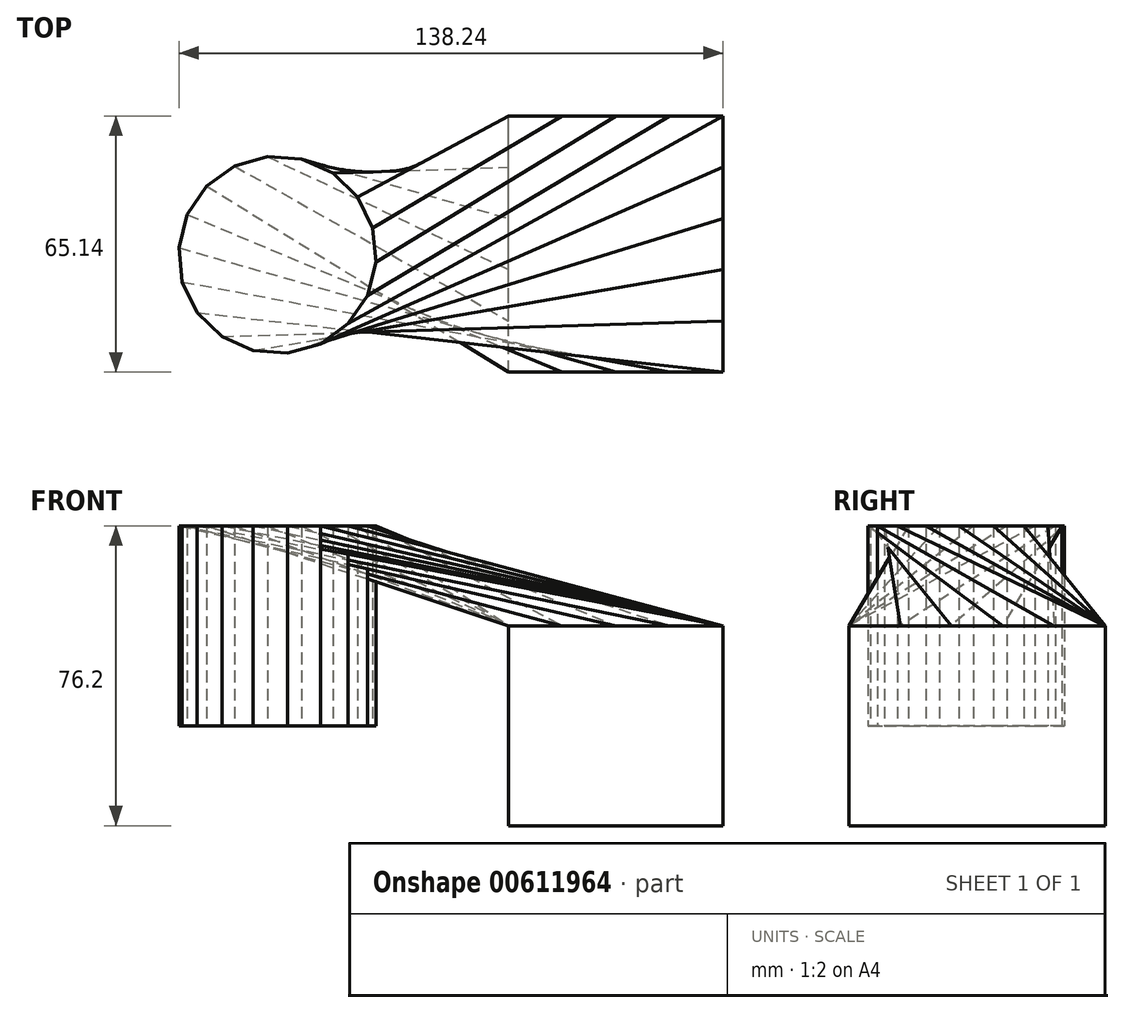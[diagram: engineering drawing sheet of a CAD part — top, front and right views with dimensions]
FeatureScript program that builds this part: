
annotation { "Feature Type Name" : "Feature", "Feature Type Description" : "" }
export const myFeature = defineFeature(function(context is Context, id is Id, definition is map)
    precondition{}
    {
        {
            var Q0;
            Q0=qCreatedBy(makeId("Top.planeOp"),FACE);
            var sketch = newSketch(context, id + "F0", { "sketchPlane" : qUnion([Q0])});
            skCircle(sketch, "E0.cCircle", {"center": v(-58.74, 24.16) * mm, "radius": 24.7 * mm, "construction": true});
            skLineSegment(sketch, "E0.0", {"start": v(-38.4, 38.84) * mm, "end": v(-34.6, 31) * mm});
            skLineSegment(sketch, "E0.1", {"start": v(-34.6, 31) * mm, "end": v(-33.73, 22.33) * mm});
            skLineSegment(sketch, "E0.2", {"start": v(-33.73, 22.33) * mm, "end": v(-35.86, 13.88) * mm});
            skLineSegment(sketch, "E0.3", {"start": v(-35.86, 13.88) * mm, "end": v(-40.76, 6.67) * mm});
            skLineSegment(sketch, "E0.4", {"start": v(-40.76, 6.67) * mm, "end": v(-47.82, 1.58) * mm});
            skLineSegment(sketch, "E0.5", {"start": v(-47.82, 1.58) * mm, "end": v(-56.2, -0.8) * mm});
            skLineSegment(sketch, "E0.6", {"start": v(-56.2, -0.8) * mm, "end": v(-64.9, -0.16) * mm});
            skLineSegment(sketch, "E0.7", {"start": v(-64.9, -0.16) * mm, "end": v(-72.84, 3.4) * mm});
            skLineSegment(sketch, "E0.8", {"start": v(-72.84, 3.4) * mm, "end": v(-79.09, 9.48) * mm});
            skLineSegment(sketch, "E0.9", {"start": v(-79.09, 9.48) * mm, "end": v(-82.88, 17.32) * mm});
            skLineSegment(sketch, "E0.10", {"start": v(-82.88, 17.32) * mm, "end": v(-83.76, 25.99) * mm});
            skLineSegment(sketch, "E0.11", {"start": v(-83.76, 25.99) * mm, "end": v(-81.63, 34.43) * mm});
            skLineSegment(sketch, "E0.12", {"start": v(-81.63, 34.43) * mm, "end": v(-76.73, 41.64) * mm});
            skLineSegment(sketch, "E0.13", {"start": v(-76.73, 41.64) * mm, "end": v(-69.67, 46.74) * mm});
            skLineSegment(sketch, "E0.14", {"start": v(-69.67, 46.74) * mm, "end": v(-61.29, 49.11) * mm});
            skLineSegment(sketch, "E0.15", {"start": v(-61.29, 49.11) * mm, "end": v(-52.6, 48.48) * mm});
            skLineSegment(sketch, "E0.16", {"start": v(-52.6, 48.48) * mm, "end": v(-44.65, 44.9) * mm});
            skLineSegment(sketch, "E0.17", {"start": v(-44.65, 44.9) * mm, "end": v(-38.4, 38.84) * mm});
            skPoint(sketch, "E0.0.midPoint", {"position": v(-36.5, 34.91) * mm});
            skLineSegment(sketch, "E1.bottom", {"start": v(48.61, 43.12) * mm, "end": v(-16.95, 43.12) * mm});
            skLineSegment(sketch, "E1.top", {"start": v(48.61, -30.81) * mm, "end": v(-16.95, -30.81) * mm});
            skLineSegment(sketch, "E1.left", {"start": v(48.61, 43.12) * mm, "end": v(48.61, -30.81) * mm});
            skLineSegment(sketch, "E1.right", {"start": v(-16.95, 43.12) * mm, "end": v(-16.95, -30.81) * mm});
            skPoint(sketch, "E1.middle", {"position": v(15.83, 6.15) * mm});
            skSolve(sketch);
        }
        {
            var Q0;
            Q0=makeQuery(id+"F0.imprint","IMPRINT",FACE,{"disambiguationData":[TD([[makeQuery(id+"F0.imprint","IMPRINT",EDGE,{"derivedFrom":sQuery(id+"F0.wireOp",EDGE,"E0.0")}),-1.0]])]});
            extrude(context, id + "F1", {"entities" : qUnion([Q0]), "depth" : 25.4 * mm, "offsetDistance" : 25.4 * mm});
        }
        {
            var Q0;
            Q0=makeQuery(id+"F1.opExtrude","CAP_FACE",FACE,{"disambiguationData":[OSD([sQuery(id+"F0.wireOp",EDGE,"E0.0"),sQuery(id+"F0.wireOp",EDGE,"E0.1"),sQuery(id+"F0.wireOp",EDGE,"E0.2"),sQuery(id+"F0.wireOp",EDGE,"E0.3"),sQuery(id+"F0.wireOp",EDGE,"E0.4"),sQuery(id+"F0.wireOp",EDGE,"E0.5"),sQuery(id+"F0.wireOp",EDGE,"E0.6"),sQuery(id+"F0.wireOp",EDGE,"E0.7"),sQuery(id+"F0.wireOp",EDGE,"E0.8"),sQuery(id+"F0.wireOp",EDGE,"E0.9"),sQuery(id+"F0.wireOp",EDGE,"E0.10"),sQuery(id+"F0.wireOp",EDGE,"E0.11"),sQuery(id+"F0.wireOp",EDGE,"E0.12"),sQuery(id+"F0.wireOp",EDGE,"E0.13"),sQuery(id+"F0.wireOp",EDGE,"E0.14"),sQuery(id+"F0.wireOp",EDGE,"E0.15"),sQuery(id+"F0.wireOp",EDGE,"E0.16"),sQuery(id+"F0.wireOp",EDGE,"E0.17")])],"isStart":false});
            extrude(context, id + "F2", {"entities" : qUnion([Q0]), "operationType" : NewBodyOperationType.ADD, "depth" : 25.4 * mm, "offsetDistance" : 25.4 * mm});
        }
        {
            var Q0;
            Q0=qCreatedBy(makeId("Top.planeOp"),FACE);
            var sketch = newSketch(context, id + "F3", { "sketchPlane" : qUnion([Q0])});
            skLineSegment(sketch, "E2.bottom", {"start": v(54.48, -5.65) * mm, "end": v(0, -5.65) * mm});
            skLineSegment(sketch, "E2.top", {"start": v(54.48, 59.49) * mm, "end": v(0, 59.49) * mm});
            skLineSegment(sketch, "E2.left", {"start": v(54.48, -5.65) * mm, "end": v(54.48, 59.49) * mm});
            skLineSegment(sketch, "E2.right", {"start": v(0, -5.65) * mm, "end": v(0, 59.49) * mm});
            skSolve(sketch);
        }
        {
            var Q0;
            Q0=makeQuery(id+"F3.imprint","IMPRINT",FACE,{"disambiguationData":[TD([[makeQuery(id+"F3.imprint","IMPRINT",EDGE,{"derivedFrom":sQuery(id+"F3.wireOp",EDGE,"E2.bottom")}),-1.0]])]});
            extrude(context, id + "F4", {"entities" : qUnion([Q0]), "depth" : 25.4 * mm, "offsetDistance" : 25.4 * mm});
        }
        {
            var Q0;
            Q0=makeQuery(id+"F2.opExtrude","CAP_FACE",FACE,{"disambiguationData":[OSD([sQuery(id+"F0.wireOp",EDGE,"E0.0"),sQuery(id+"F0.wireOp",EDGE,"E0.1"),sQuery(id+"F0.wireOp",EDGE,"E0.2"),sQuery(id+"F0.wireOp",EDGE,"E0.3"),sQuery(id+"F0.wireOp",EDGE,"E0.4"),sQuery(id+"F0.wireOp",EDGE,"E0.5"),sQuery(id+"F0.wireOp",EDGE,"E0.6"),sQuery(id+"F0.wireOp",EDGE,"E0.7"),sQuery(id+"F0.wireOp",EDGE,"E0.8"),sQuery(id+"F0.wireOp",EDGE,"E0.9"),sQuery(id+"F0.wireOp",EDGE,"E0.10"),sQuery(id+"F0.wireOp",EDGE,"E0.11"),sQuery(id+"F0.wireOp",EDGE,"E0.12"),sQuery(id+"F0.wireOp",EDGE,"E0.13"),sQuery(id+"F0.wireOp",EDGE,"E0.14"),sQuery(id+"F0.wireOp",EDGE,"E0.15"),sQuery(id+"F0.wireOp",EDGE,"E0.16"),sQuery(id+"F0.wireOp",EDGE,"E0.17")])],"isStart":false});
            var Q1;
            Q1=makeQuery(id+"F4.opExtrude","CAP_FACE",FACE,{"disambiguationData":[OSD([sQuery(id+"F3.wireOp",EDGE,"E2.bottom"),sQuery(id+"F3.wireOp",EDGE,"E2.top"),sQuery(id+"F3.wireOp",EDGE,"E2.left"),sQuery(id+"F3.wireOp",EDGE,"E2.right")])],"isStart":false});
            loft(context, id + "F5", {"sheetProfilesArray" : [{ "sheetProfileEntities" : qUnion([Q0]) }, { "sheetProfileEntities" : qUnion([Q1]) }]});
        }
        {
            var Q0;
            Q0=makeQuery(id+"F4.opExtrude","CAP_FACE",FACE,{"disambiguationData":[OSD([sQuery(id+"F3.wireOp",EDGE,"E2.bottom"),sQuery(id+"F3.wireOp",EDGE,"E2.top"),sQuery(id+"F3.wireOp",EDGE,"E2.left"),sQuery(id+"F3.wireOp",EDGE,"E2.right")])],"isStart":true});
            extrude(context, id + "F6", {"entities" : qUnion([Q0]), "operationType" : NewBodyOperationType.ADD, "depth" : 25.4 * mm, "offsetDistance" : 25.4 * mm});
        }
    });
